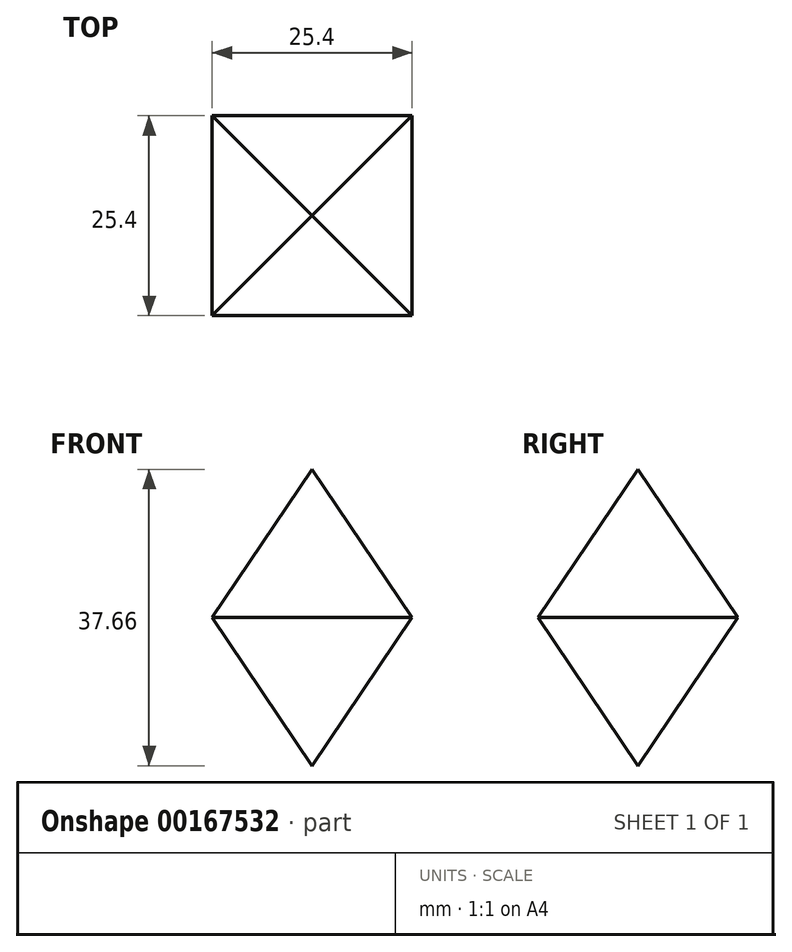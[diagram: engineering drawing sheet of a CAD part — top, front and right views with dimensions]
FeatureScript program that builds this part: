
annotation { "Feature Type Name" : "Feature", "Feature Type Description" : "" }
export const myFeature = defineFeature(function(context is Context, id is Id, definition is map)
    precondition{}
    {
        {
            var Q0;
            Q0=qCreatedBy(makeId("Top.planeOp"),FACE);
            var sketch = newSketch(context, id + "F0", { "sketchPlane" : qUnion([Q0])});
            skCircle(sketch, "E0.cCircle", {"center": v(0, 0) * mm, "radius": 12.7 * mm, "construction": true});
            skLineSegment(sketch, "E0.0", {"start": v(12.7, 12.7) * mm, "end": v(12.7, -12.7) * mm});
            skLineSegment(sketch, "E0.1", {"start": v(12.7, -12.7) * mm, "end": v(-12.7, -12.7) * mm});
            skLineSegment(sketch, "E0.2", {"start": v(-12.7, -12.7) * mm, "end": v(-12.7, 12.7) * mm});
            skLineSegment(sketch, "E0.3", {"start": v(-12.7, 12.7) * mm, "end": v(12.7, 12.7) * mm});
            skPoint(sketch, "E0.0.midPoint", {"position": v(12.7, 0) * mm});
            skSolve(sketch);
        }
        {
            var Q0;
            Q0=makeQuery(id+"F0.imprint","IMPRINT",FACE,{"disambiguationData":[TD([[makeQuery(id+"F0.imprint","IMPRINT",EDGE,{"derivedFrom":sQuery(id+"F0.wireOp",EDGE,"E0.0")}),-1.0]])]});
            extrude(context, id + "F1", {"entities" : qUnion([Q0]), "depth" : 29.46 * mm, "hasDraft" : true, "draftAngle" : 34 * degree, "draftPullDirection" : true});
        }
        {
            var Q0;
            Q0=makeQuery(id+"F1.opExtrude","CAP_FACE",FACE,{"disambiguationData":[OSD([sQuery(id+"F0.wireOp",EDGE,"E0.0"),sQuery(id+"F0.wireOp",EDGE,"E0.1"),sQuery(id+"F0.wireOp",EDGE,"E0.2"),sQuery(id+"F0.wireOp",EDGE,"E0.3")])],"isStart":true});
            extrude(context, id + "F2", {"entities" : qUnion([Q0]), "operationType" : NewBodyOperationType.ADD, "depth" : 31.2 * mm, "hasDraft" : true, "draftAngle" : 34 * degree, "draftPullDirection" : true});
        }
    });
